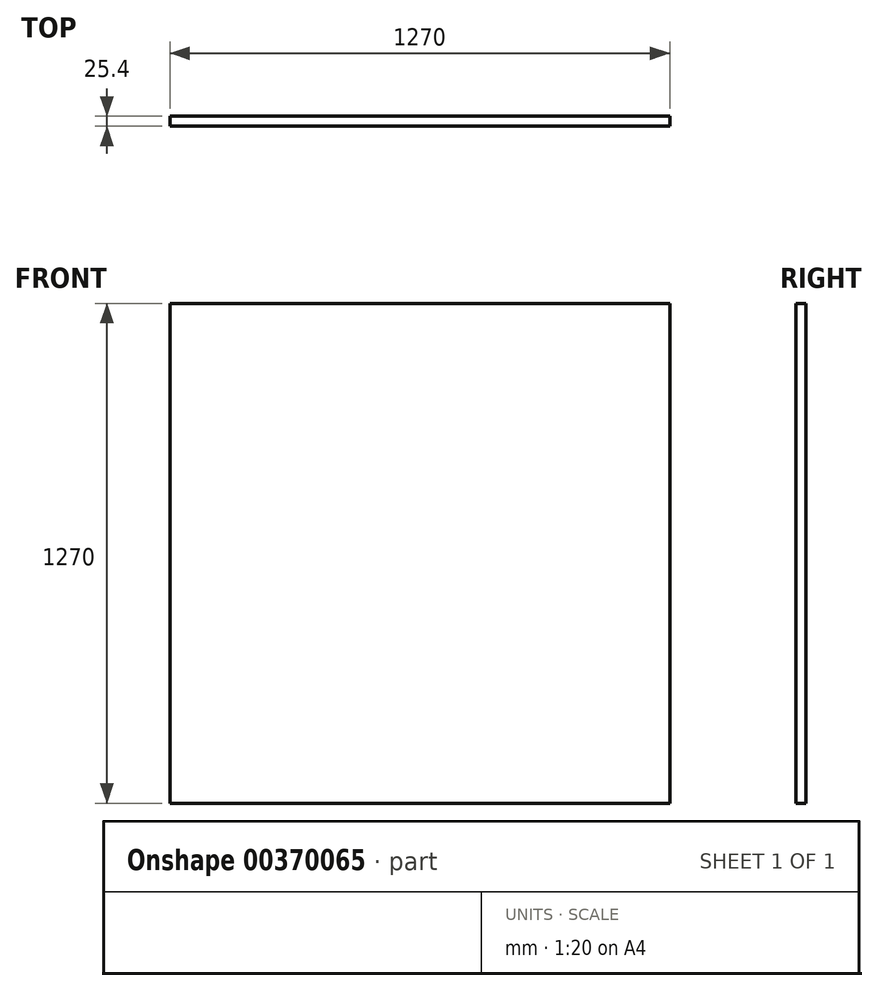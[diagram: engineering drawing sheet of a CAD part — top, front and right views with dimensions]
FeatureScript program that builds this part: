
annotation { "Feature Type Name" : "Feature", "Feature Type Description" : "" }
export const myFeature = defineFeature(function(context is Context, id is Id, definition is map)
    precondition{}
    {
        {
            var Q0;
            Q0=qCreatedBy(makeId("Front.planeOp"),FACE);
            var sketch = newSketch(context, id + "F0", { "sketchPlane" : qUnion([Q0])});
            skLineSegment(sketch, "E0.bottom", {"start": v(0, 635) * mm, "end": v(-1270, 635) * mm});
            skLineSegment(sketch, "E0.top", {"start": v(0, -635) * mm, "end": v(-1270, -635) * mm});
            skLineSegment(sketch, "E0.left", {"start": v(0, 635) * mm, "end": v(0, -635) * mm});
            skLineSegment(sketch, "E0.right", {"start": v(-1270, 635) * mm, "end": v(-1270, -635) * mm});
            skPoint(sketch, "E0.middle", {"position": v(-635, 0) * mm});
            skSolve(sketch);
        }
        {
            var Q0;
            Q0 = qSketchRegion(id + "F0", true);
            extrude(context, id + "F1", {"entities" : qUnion([Q0]), "depth" : 25.4 * mm});
        }
    });
